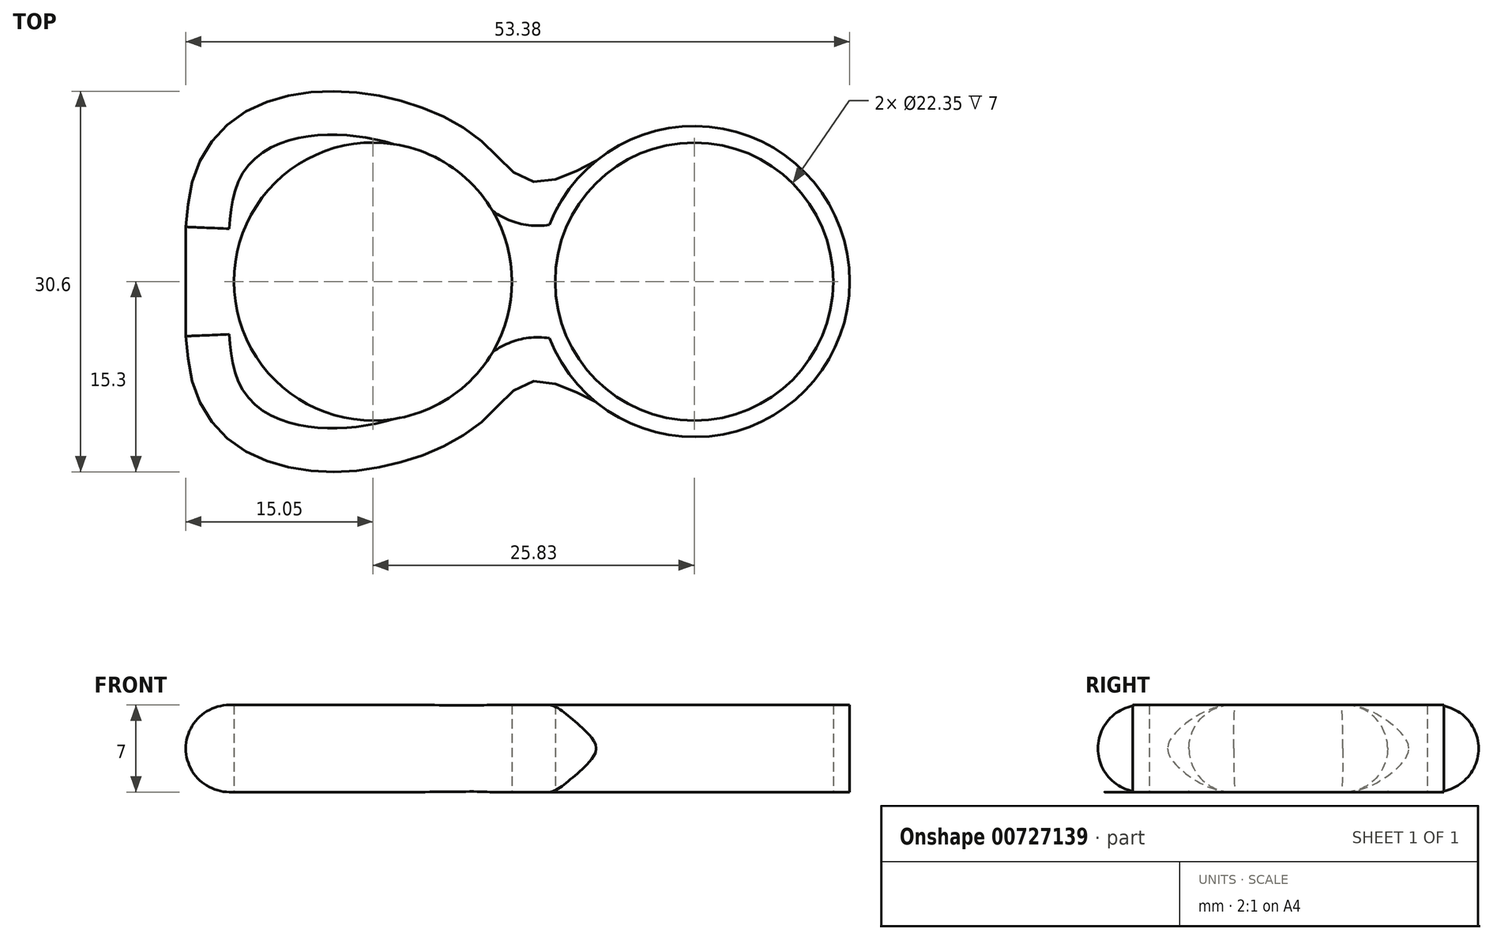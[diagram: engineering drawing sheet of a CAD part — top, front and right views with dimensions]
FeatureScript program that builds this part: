
annotation { "Feature Type Name" : "Feature", "Feature Type Description" : "" }
export const myFeature = defineFeature(function(context is Context, id is Id, definition is map)
    precondition{}
    {
        {
            var Q0;
            Q0=qCreatedBy(makeId("Top.planeOp"),FACE);
            var sketch = newSketch(context, id + "F0", { "sketchPlane" : qUnion([Q0])});
            skCircle(sketch, "E0", {"center": v(0, 0) * mm, "radius": 12.5 * mm});
            skCircle(sketch, "E1", {"center": v(0, 0) * mm, "radius": 11.18 * mm});
            skLineSegment(sketch, "E2", {"start": v(0, 0) * mm, "end": v(-35, 0) * mm});
            skCircle(sketch, "E3", {"center": v(-25.83, 0) * mm, "radius": 11.18 * mm});
            skFitSpline(sketch, "E4", {"points": [v(-7.89, 9.7) * mm, v(-13.23, 8.07) * mm, v(-17.43, 11.57) * mm, v(-27.58, 15.24) * mm, v(-36.33, 13.5) * mm, v(-40, 9.12) * mm, v(-40.88, 4.4) * mm], "startDerivative": vector(-38.3, -19.72) * mm, "endDerivative": vector(-2.87, -33.99) * mm});
            skFitSpline(sketch, "E5.MirrorCS", {"points": [v(-7.89, -9.7) * mm, v(-13.23, -8.07) * mm, v(-17.43, -11.57) * mm, v(-27.58, -15.24) * mm, v(-36.33, -13.5) * mm, v(-40, -9.12) * mm, v(-40.88, -4.4) * mm], "startDerivative": vector(-38.3, 19.72) * mm, "endDerivative": vector(-2.87, 33.99) * mm});
            skLineSegment(sketch, "E6", {"start": v(-40.88, 4.4) * mm, "end": v(-40.88, -4.4) * mm});
            skSolve(sketch);
        }
        {
            var Q0;
            Q0=makeQuery(id+"F0.imprint","IMPRINT",FACE,{"disambiguationData":[TD([[makeQuery(id+"F0.imprint","IMPRINT",EDGE,{"derivedFrom":sQuery(id+"F0.wireOp",EDGE,"E3")}),-1.0]])]});
            var Q1;
            Q1=makeQuery(id+"F0.imprint","IMPRINT",FACE,{"disambiguationData":[TD([[makeQuery(id+"F0.imprint","IMPRINT",EDGE,{"derivedFrom":sQuery(id+"F0.wireOp",EDGE,"E1")}),-1.0]])]});
            extrude(context, id + "F1", {"entities" : qUnion([Q0, Q1]), "depth" : 7 * mm, "offsetDistance" : 25.4 * mm});
        }
        {
            var Q0;
            Q0=makeQuery(id+"F1.opExtrude","CAP_EDGE",EDGE,{"disambiguationData":[OSD([sQuery(id+"F0.wireOp",EDGE,"E5.MirrorCS")])],"isStart":false});
            var Q1;
            Q1=makeQuery(id+"F1.opExtrude","CAP_EDGE",EDGE,{"disambiguationData":[OSD([sQuery(id+"F0.wireOp",EDGE,"E5.MirrorCS")])],"isStart":true});
            var Q2;
            Q2=makeQuery(id+"F1.opExtrude","CAP_EDGE",EDGE,{"disambiguationData":[OSD([sQuery(id+"F0.wireOp",EDGE,"E4")])],"isStart":false});
            var Q3;
            Q3=makeQuery(id+"F1.opExtrude","CAP_EDGE",EDGE,{"disambiguationData":[OSD([sQuery(id+"F0.wireOp",EDGE,"E4")])],"isStart":true});
            var Q4;
            Q4=makeQuery(id+"F1.opExtrude","CAP_EDGE",EDGE,{"disambiguationData":[OSD([sQuery(id+"F0.wireOp",EDGE,"E6")])],"isStart":false});
            var Q5;
            Q5=makeQuery(id+"F1.opExtrude","CAP_EDGE",EDGE,{"disambiguationData":[OSD([sQuery(id+"F0.wireOp",EDGE,"E6")])],"isStart":true});
            fillet(context, id + "F2", {"entities" : qUnion([Q0, Q1, Q2, Q3, Q4, Q5]), "radius" : 3.5 * mm, "tangentPropagation" : true, "allowEdgeOverflow" : false});
        }
    });
